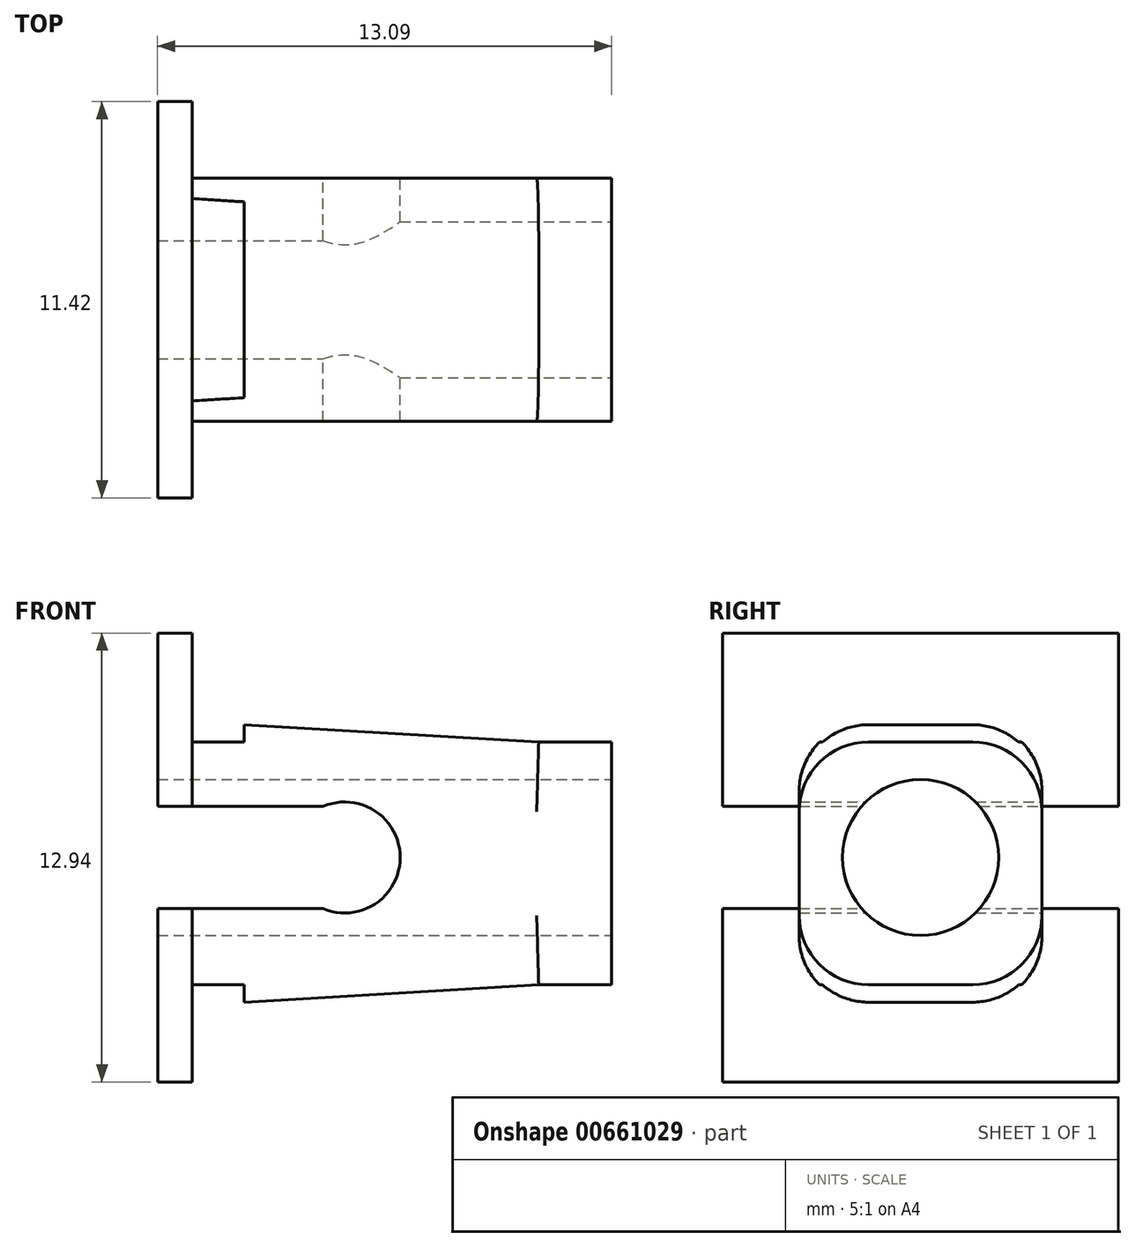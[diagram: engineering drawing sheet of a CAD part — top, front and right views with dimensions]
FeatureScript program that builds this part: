
annotation { "Feature Type Name" : "Feature", "Feature Type Description" : "" }
export const myFeature = defineFeature(function(context is Context, id is Id, definition is map)
    precondition{}
    {
        {
            var Q0;
            Q0=qCreatedBy(makeId("Front.planeOp"),FACE);
            var sketch = newSketch(context, id + "F0", { "sketchPlane" : qUnion([Q0])});
            skLineSegment(sketch, "E0", {"start": v(-5.76, 1.47) * mm, "end": v(-5.76, 6.47) * mm});
            skLineSegment(sketch, "E1", {"start": v(-5.76, 6.47) * mm, "end": v(-4.76, 6.47) * mm});
            skLineSegment(sketch, "E2", {"start": v(-4.76, 6.47) * mm, "end": v(-4.76, 3.33) * mm});
            skLineSegment(sketch, "E3", {"start": v(-4.76, 3.33) * mm, "end": v(-3.26, 3.33) * mm});
            skLineSegment(sketch, "E4", {"start": v(-3.26, 3.33) * mm, "end": v(-3.26, 3.83) * mm});
            skLineSegment(sketch, "E5", {"start": v(-3.26, 3.83) * mm, "end": v(5.23, 3.33) * mm});
            skLineSegment(sketch, "E6", {"start": v(5.23, 3.33) * mm, "end": v(7.33, 3.33) * mm});
            skLineSegment(sketch, "E7", {"start": v(7.33, 3.33) * mm, "end": v(7.33, -3.67) * mm});
            skLineSegment(sketch, "E8", {"start": v(7.33, -3.67) * mm, "end": v(5.23, -3.67) * mm});
            skLineSegment(sketch, "E9", {"start": v(5.23, -3.67) * mm, "end": v(-3.26, -4.17) * mm});
            skLineSegment(sketch, "E10", {"start": v(-3.26, -4.17) * mm, "end": v(-3.26, -3.67) * mm});
            skLineSegment(sketch, "E11", {"start": v(-3.26, -3.67) * mm, "end": v(-4.76, -3.67) * mm});
            skLineSegment(sketch, "E12", {"start": v(-4.76, -3.67) * mm, "end": v(-4.76, -6.47) * mm});
            skLineSegment(sketch, "E13", {"start": v(-4.76, -6.47) * mm, "end": v(-5.76, -6.47) * mm});
            skLineSegment(sketch, "E14", {"start": v(-5.76, -6.47) * mm, "end": v(-5.76, -1.47) * mm});
            skLineSegment(sketch, "E15", {"start": v(-5.76, -1.47) * mm, "end": v(-1, -1.47) * mm});
            skLineSegment(sketch, "E16", {"start": v(-1, 1.47) * mm, "end": v(-5.76, 1.47) * mm});
            skArc(sketch, "E17", {"start": v(-1, -1.47) * mm, "mid": v(1.24, 0) * mm, "end": v(-1, 1.47) * mm});
            skPoint(sketch, "E17.centerSnap0", {"position": v(-0.16, 0) * mm});
            skLineSegment(sketch, "E18", {"start": v(-4.76, -3.67) * mm, "end": v(-4.76, -1.47) * mm});
            skLineSegment(sketch, "E19", {"start": v(-4.76, 3.33) * mm, "end": v(-4.76, 1.47) * mm});
            skPoint(sketch, "E20.orphan", {"position": v(-0.16, 1.47) * mm});
            skPoint(sketch, "E21.orphan", {"position": v(-0.16, -1.47) * mm});
            skSolve(sketch);
        }
        {
            var Q0;
            {var subQ2=sQuery(id+"F0.wireOp",EDGE,"E0");Q0=makeQuery(id+"F0.imprint","IMPRINT",FACE,{"disambiguationData":[TD([[makeQuery(id+"F0.imprint","IMPRINT",EDGE,{"derivedFrom":subQ2}),-1.0]])]});}
            var Q1;
            Q1=makeQuery(id+"F0.imprint","IMPRINT",FACE,{"disambiguationData":[TD([[makeQuery(id+"F0.imprint","IMPRINT",EDGE,{"derivedFrom":sQuery(id+"F0.wireOp",EDGE,"E12")}),-1.0]])]});
            extrude(context, id + "F1", {"entities" : qUnion([Q0, Q1]), "endBound" : BoundingType.SYMMETRIC, "depth" : 11.42 * mm, "offsetDistance" : 25 * mm});
        }
        {
            var Q0;
            Q0=makeQuery(id+"F0.imprint","IMPRINT",FACE,{"disambiguationData":[TD([[makeQuery(id+"F0.imprint","IMPRINT",EDGE,{"derivedFrom":sQuery(id+"F0.wireOp",EDGE,"E3")}),-1.0]])]});
            extrude(context, id + "F2", {"entities" : qUnion([Q0]), "operationType" : NewBodyOperationType.ADD, "endBound" : BoundingType.SYMMETRIC, "depth" : 7 * mm, "offsetDistance" : 25 * mm});
        }
        {
            var Q0;
            Q0=qCreatedBy(makeId("Right.planeOp"),FACE);
            var sketch = newSketch(context, id + "F3", { "sketchPlane" : qUnion([Q0])});
            skCircle(sketch, "E22", {"center": v(0, 0) * mm, "radius": 2.25 * mm});
            skSolve(sketch);
        }
        {
            var Q0;
            Q0=makeQuery(id+"F3.imprint","IMPRINT",FACE,{"disambiguationData":[TD([[makeQuery(id+"F3.imprint","IMPRINT",EDGE,{"derivedFrom":sQuery(id+"F3.wireOp",EDGE,"E22")}),1.0]])]});
            var Q1;
            Q1=sQuery(id+"F3.wireOp",EDGE,"E22");
            extrude(context, id + "F4", {"entities" : qUnion([Q0]), "operationType" : NewBodyOperationType.REMOVE, "surfaceEntities" : qUnion([Q1]), "endBound" : BoundingType.SYMMETRIC, "oppositeDirection" : true, "depth" : 18.8 * mm, "offsetDistance" : 25 * mm});
        }
        {
            var Q0;
            Q0=makeQuery(id+"F2.opExtrude","CAP_EDGE",EDGE,{"disambiguationData":[OSD([sQuery(id+"F0.wireOp",EDGE,"E5")])],"isStart":true});
            var Q1;
            Q1=makeQuery(id+"F2.opExtrude","CAP_EDGE",EDGE,{"disambiguationData":[OSD([sQuery(id+"F0.wireOp",EDGE,"E6")])],"isStart":true});
            var Q2;
            Q2=makeQuery(id+"F2.opExtrude","CAP_EDGE",EDGE,{"disambiguationData":[OSD([sQuery(id+"F0.wireOp",EDGE,"E5")])],"isStart":false});
            var Q3;
            Q3=makeQuery(id+"F2.opExtrude","CAP_EDGE",EDGE,{"disambiguationData":[OSD([sQuery(id+"F0.wireOp",EDGE,"E6")])],"isStart":false});
            var Q4;
            Q4=makeQuery(id+"F2.opExtrude","CAP_EDGE",EDGE,{"disambiguationData":[OSD([sQuery(id+"F0.wireOp",EDGE,"E9")])],"isStart":false});
            var Q5;
            Q5=makeQuery(id+"F2.opExtrude","CAP_EDGE",EDGE,{"disambiguationData":[OSD([sQuery(id+"F0.wireOp",EDGE,"E8")])],"isStart":false});
            var Q6;
            Q6=makeQuery(id+"F2.opExtrude","CAP_EDGE",EDGE,{"disambiguationData":[OSD([sQuery(id+"F0.wireOp",EDGE,"E9")])],"isStart":true});
            var Q7;
            Q7=makeQuery(id+"F2.opExtrude","CAP_EDGE",EDGE,{"disambiguationData":[OSD([sQuery(id+"F0.wireOp",EDGE,"E8")])],"isStart":true});
            fillet(context, id + "F5", {"entities" : qUnion([Q0, Q1, Q2, Q3, Q4, Q5, Q6, Q7]), "radius" : 2 * mm, "tangentPropagation" : true, "allowEdgeOverflow" : false});
        }
    });
